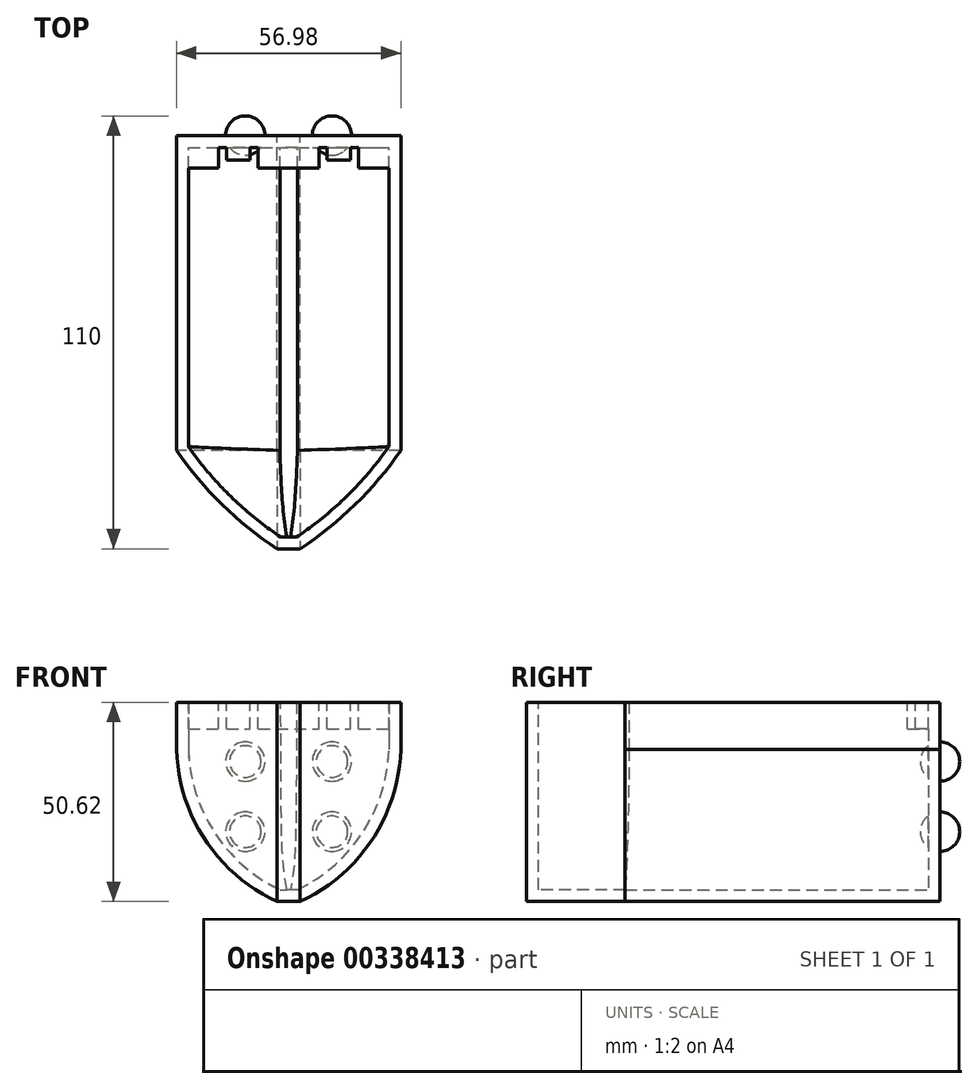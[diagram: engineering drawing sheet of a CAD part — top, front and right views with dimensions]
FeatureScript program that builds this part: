
annotation { "Feature Type Name" : "Feature", "Feature Type Description" : "" }
export const myFeature = defineFeature(function(context is Context, id is Id, definition is map)
    precondition{}
    {
        {
            var Q0;
            Q0=qCreatedBy(makeId("Front.planeOp"),FACE);
            var sketch = newSketch(context, id + "F0", { "sketchPlane" : qUnion([Q0])});
            skLineSegment(sketch, "E0.bottom", {"start": v(0, 23.95) * mm, "end": v(-28.49, 23.95) * mm});
            skLineSegment(sketch, "E0.top", {"start": v(0, -26.67) * mm, "end": v(-2.9, -26.67) * mm});
            skLineSegment(sketch, "E0.right", {"start": v(-28.49, 23.95) * mm, "end": v(-28.49, 11.98) * mm});
            skArc(sketch, "E1", {"start": v(-28.49, 11.98) * mm, "mid": v(-21.19, -10.99) * mm, "end": v(-2.9, -26.67) * mm});
            skArc(sketch, "E2.MirrorCS", {"start": v(28.49, 11.98) * mm, "mid": v(21.19, -10.99) * mm, "end": v(2.9, -26.67) * mm});
            skLineSegment(sketch, "E3.MirrorCS", {"start": v(28.49, 23.95) * mm, "end": v(28.49, 11.98) * mm});
            skLineSegment(sketch, "E4.MirrorCS", {"start": v(0, 23.95) * mm, "end": v(28.49, 23.95) * mm});
            skLineSegment(sketch, "E5.MirrorCS", {"start": v(0, -26.67) * mm, "end": v(2.9, -26.67) * mm});
            skPoint(sketch, "E6.orphan", {"position": v(-28.49, -26.67) * mm});
            skPoint(sketch, "E7.orphan", {"position": v(28.49, -26.67) * mm});
            skSolve(sketch);
        }
        {
            var Q0;
            Q0=makeQuery(id+"F0.imprint","IMPRINT",FACE,{"disambiguationData":[TD([[makeQuery(id+"F0.imprint","IMPRINT",EDGE,{"derivedFrom":sQuery(id+"F0.wireOp",EDGE,"E0.bottom")}),1.0]])]});
            extrude(context, id + "F1", {"entities" : qUnion([Q0]), "depth" : 80 * mm});
        }
        {
            var Q0;
            Q0=makeQuery(id+"F1.opExtrude","CAP_FACE",FACE,{"disambiguationData":[OSD([sQuery(id+"F0.wireOp",EDGE,"E0.bottom"),sQuery(id+"F0.wireOp",EDGE,"E0.top"),sQuery(id+"F0.wireOp",EDGE,"E0.right"),sQuery(id+"F0.wireOp",EDGE,"E1"),sQuery(id+"F0.wireOp",EDGE,"E2.MirrorCS"),sQuery(id+"F0.wireOp",EDGE,"E3.MirrorCS"),sQuery(id+"F0.wireOp",EDGE,"E4.MirrorCS"),sQuery(id+"F0.wireOp",EDGE,"E5.MirrorCS")])],"isStart":false});
            cPlane(context, id + "F2", {"entities" : qUnion([Q0]), "cplaneType" : CPlaneType.OFFSET, "offset" : 25 * mm, "width" : 150 * mm, "height" : 150 * mm});
        }
        {
            var Q0;
            Q0=qCreatedBy(id+"F2.planeOp",FACE);
            var sketch = newSketch(context, id + "F3", { "sketchPlane" : qUnion([Q0])});
            skLineSegment(sketch, "E8.bottom", {"start": v(0, -26.67) * mm, "end": v(-2.9, -26.67) * mm});
            skLineSegment(sketch, "E8.top", {"start": v(0, 23.95) * mm, "end": v(-2.9, 23.95) * mm});
            skLineSegment(sketch, "E8.right", {"start": v(-2.9, -26.67) * mm, "end": v(-2.9, 23.95) * mm});
            skLineSegment(sketch, "E9.MirrorCS", {"start": v(2.9, -26.67) * mm, "end": v(2.9, 23.95) * mm});
            skLineSegment(sketch, "E10.MirrorCS", {"start": v(0, -26.67) * mm, "end": v(2.9, -26.67) * mm});
            skLineSegment(sketch, "E11.MirrorCS", {"start": v(0, 23.95) * mm, "end": v(2.9, 23.95) * mm});
            skSolve(sketch);
        }
        {
            var Q0;
            Q0=makeQuery(id+"F1.opExtrude","SWEPT_FACE",FACE,{"disambiguationData":[OSD([sQuery(id+"F0.wireOp",EDGE,"E0.bottom"),sQuery(id+"F0.wireOp",EDGE,"E4.MirrorCS")])]});
            cPlane(context, id + "F4", {"entities" : qUnion([Q0]), "cplaneType" : CPlaneType.OFFSET, "offset" : 0 * mm, "width" : 150 * mm, "height" : 150 * mm});
        }
        {
            var Q0;
            Q0=qCreatedBy(id+"F4.planeOp",FACE);
            var sketch = newSketch(context, id + "F5", { "sketchPlane" : qUnion([Q0])});
            skArc(sketch, "E12", {"start": v(-28.49, -80) * mm, "mid": v(-16.9, -93.73) * mm, "end": v(-2.9, -105) * mm});
            skLineSegment(sketch, "E13", {"start": v(0, -105.03) * mm, "end": v(0, -80.6) * mm, "construction": true});
            skArc(sketch, "E14.MirrorCS", {"start": v(28.49, -80) * mm, "mid": v(16.9, -93.73) * mm, "end": v(2.9, -105) * mm});
            skSolve(sketch);
        }
        {
            var Q0;
            Q0=makeQuery(id+"F1.opExtrude","SWEPT_FACE",FACE,{"disambiguationData":[OSD([sQuery(id+"F0.wireOp",EDGE,"E0.top"),sQuery(id+"F0.wireOp",EDGE,"E5.MirrorCS")])]});
            cPlane(context, id + "F6", {"entities" : qUnion([Q0]), "cplaneType" : CPlaneType.OFFSET, "offset" : 0 * mm, "width" : 150 * mm, "height" : 150 * mm});
        }
        {
            var Q0;
            Q0=qCreatedBy(id+"F6.planeOp",FACE);
            var sketch = newSketch(context, id + "F7", { "sketchPlane" : qUnion([Q0])});
            skLineSegment(sketch, "E15", {"start": v(-2.9, 80) * mm, "end": v(-2.9, 105) * mm});
            skLineSegment(sketch, "E16", {"start": v(2.9, 80) * mm, "end": v(2.9, 105) * mm});
            skSolve(sketch);
        }
        {
            var Q1;
            Q1=makeQuery(id+"F1.opExtrude","CAP_FACE",FACE,{"disambiguationData":[OSD([sQuery(id+"F0.wireOp",EDGE,"E0.bottom"),sQuery(id+"F0.wireOp",EDGE,"E0.top"),sQuery(id+"F0.wireOp",EDGE,"E0.right"),sQuery(id+"F0.wireOp",EDGE,"E1"),sQuery(id+"F0.wireOp",EDGE,"E2.MirrorCS"),sQuery(id+"F0.wireOp",EDGE,"E3.MirrorCS"),sQuery(id+"F0.wireOp",EDGE,"E4.MirrorCS"),sQuery(id+"F0.wireOp",EDGE,"E5.MirrorCS")])],"isStart":false});
            var Q2;
            Q2=makeQuery(id+"F3.imprint","IMPRINT",FACE,{"disambiguationData":[TD([[makeQuery(id+"F3.imprint","IMPRINT",EDGE,{"derivedFrom":sQuery(id+"F3.wireOp",EDGE,"E8.bottom")}),-1.0]])]});
            var Q3;
            Q3=sQuery(id+"F5.wireOp",EDGE,"E12");
            var Q4;
            Q4=sQuery(id+"F5.wireOp",EDGE,"E14.MirrorCS");
            var Q5;
            Q5=sQuery(id+"F7.wireOp",EDGE,"E16");
            var Q6;
            Q6=sQuery(id+"F7.wireOp",EDGE,"E15");
            loft(context, id + "F8", {"operationType" : NewBodyOperationType.ADD, "addGuides" : true, "sheetProfilesArray" : [{ "sheetProfileEntities" : qUnion([Q1]) }, { "sheetProfileEntities" : qUnion([Q2]) }], "guidesArray" : [{ "guideEntities" : qUnion([Q3]), "guideDerivativeType" : LoftGuideDerivativeType.DEFAULT, "guideDerivativeMagnitude" : 1 }, { "guideEntities" : qUnion([Q4]), "guideDerivativeType" : LoftGuideDerivativeType.DEFAULT, "guideDerivativeMagnitude" : 1 }, { "guideEntities" : qUnion([Q5]), "guideDerivativeType" : LoftGuideDerivativeType.DEFAULT, "guideDerivativeMagnitude" : 1 }, { "guideEntities" : qUnion([Q6]), "guideDerivativeType" : LoftGuideDerivativeType.DEFAULT, "guideDerivativeMagnitude" : 1 }]});
        }
        {
            var Q0;
            {var subQ0=sQuery(id+"F0.wireOp",EDGE,"E4.MirrorCS");var subQ1=sQuery(id+"F0.wireOp",EDGE,"E0.bottom");Q0=makeQuery(id+"F8.boolean.opBoolean","MERGE",FACE,{"derivedFrom":[makeQuery(id+"F1.opExtrude","SWEPT_FACE",FACE,{"disambiguationData":[OSD([subQ1,subQ0])]}),makeQuery(id+"F8.opLoft","SWEPT_FACE",FACE,{"disambiguationData":[OSD([subQ1,subQ0,sQuery(id+"F3.wireOp",EDGE,"E8.top"),sQuery(id+"F3.wireOp",EDGE,"E11.MirrorCS"),sQuery(id+"F5.wireOp",EDGE,"E14.MirrorCS")])]})]});}
            shell(context, id + "F9", {"entities" : qUnion([Q0]), "thickness" : 3 * mm});
        }
        {
            var Q0;
            {var subQ0=sQuery(id+"F0.wireOp",EDGE,"E4.MirrorCS");var subQ1=sQuery(id+"F0.wireOp",EDGE,"E0.bottom");Q0=makeQuery(id+"F8.boolean.opBoolean","MERGE",FACE,{"derivedFrom":[makeQuery(id+"F1.opExtrude","SWEPT_FACE",FACE,{"disambiguationData":[OSD([subQ1,subQ0])]}),makeQuery(id+"F8.opLoft","SWEPT_FACE",FACE,{"disambiguationData":[OSD([subQ1,subQ0,sQuery(id+"F3.wireOp",EDGE,"E8.top"),sQuery(id+"F3.wireOp",EDGE,"E11.MirrorCS"),sQuery(id+"F5.wireOp",EDGE,"E14.MirrorCS")])]})]});}
            var sketch = newSketch(context, id + "F10", { "sketchPlane" : qUnion([Q0])});
            skLineSegment(sketch, "E17.bottom", {"start": v(-25.49, -3) * mm, "end": v(25.49, -3) * mm});
            skLineSegment(sketch, "E17.top", {"start": v(-25.49, -8.24) * mm, "end": v(25.49, -8.24) * mm});
            skLineSegment(sketch, "E17.left", {"start": v(-25.49, -3) * mm, "end": v(-25.49, -8.24) * mm});
            skLineSegment(sketch, "E17.right", {"start": v(25.49, -3) * mm, "end": v(25.49, -8.24) * mm});
            skSolve(sketch);
        }
        {
            var Q0;
            Q0=makeQuery(id+"F10.imprint","IMPRINT",FACE,{"disambiguationData":[TD([[makeQuery(id+"F10.imprint","IMPRINT",EDGE,{"derivedFrom":sQuery(id+"F10.wireOp",EDGE,"E17.bottom")}),-1.0]])]});
            extrude(context, id + "F11", {"entities" : qUnion([Q0]), "operationType" : NewBodyOperationType.ADD, "oppositeDirection" : true, "depth" : 6.8 * mm});
        }
        {
            var Q0;
            {var subQ0=sQuery(id+"F0.wireOp",EDGE,"E4.MirrorCS");var subQ1=sQuery(id+"F0.wireOp",EDGE,"E0.bottom");Q0=makeQuery(id+"F11.boolean.opBoolean","MERGE",FACE,{"derivedFrom":[makeQuery(id+"F8.boolean.opBoolean","MERGE",FACE,{"derivedFrom":[makeQuery(id+"F1.opExtrude","SWEPT_FACE",FACE,{"disambiguationData":[OSD([subQ1,subQ0])]}),makeQuery(id+"F8.opLoft","SWEPT_FACE",FACE,{"disambiguationData":[OSD([subQ1,subQ0,sQuery(id+"F3.wireOp",EDGE,"E8.top"),sQuery(id+"F3.wireOp",EDGE,"E11.MirrorCS"),sQuery(id+"F5.wireOp",EDGE,"E14.MirrorCS")])]})]}),makeQuery(id+"F11.opExtrude","CAP_FACE",FACE,{"disambiguationData":[OSD([sQuery(id+"F10.wireOp",EDGE,"E17.bottom"),sQuery(id+"F10.wireOp",EDGE,"E17.top"),sQuery(id+"F10.wireOp",EDGE,"E17.left"),sQuery(id+"F10.wireOp",EDGE,"E17.right")])],"isStart":true})]});}
            var sketch = newSketch(context, id + "F12", { "sketchPlane" : qUnion([Q0])});
            skLineSegment(sketch, "E18", {"start": v(0, 0) * mm, "end": v(0, -30.47) * mm, "construction": true});
            skPoint(sketch, "E18.endSnap0", {"position": v(0, 0) * mm});
            skLineSegment(sketch, "E19.bottom", {"start": v(-7.74, -8.24) * mm, "end": v(-17.74, -8.24) * mm});
            skLineSegment(sketch, "E19.top", {"start": v(-7.74, -3) * mm, "end": v(-9.74, -3) * mm});
            skLineSegment(sketch, "E19.left", {"start": v(-7.74, -8.24) * mm, "end": v(-7.74, -3) * mm});
            skLineSegment(sketch, "E19.right", {"start": v(-17.74, -8.24) * mm, "end": v(-17.74, -3) * mm});
            skLineSegment(sketch, "E20.top", {"start": v(-9.74, -6.24) * mm, "end": v(-15.74, -6.24) * mm});
            skLineSegment(sketch, "E20.left", {"start": v(-9.74, -3) * mm, "end": v(-9.74, -6.24) * mm});
            skLineSegment(sketch, "E20.right", {"start": v(-15.74, -3) * mm, "end": v(-15.74, -6.24) * mm});
            skLineSegment(sketch, "E21.trimOffspring", {"start": v(-15.74, -3) * mm, "end": v(-17.74, -3) * mm});
            skLineSegment(sketch, "E22.MirrorCS", {"start": v(7.74, -8.24) * mm, "end": v(7.74, -3) * mm});
            skLineSegment(sketch, "E23.MirrorCS", {"start": v(7.74, -3) * mm, "end": v(9.74, -3) * mm});
            skLineSegment(sketch, "E24.MirrorCS", {"start": v(9.74, -3) * mm, "end": v(9.74, -6.24) * mm});
            skLineSegment(sketch, "E25.MirrorCS", {"start": v(9.74, -6.24) * mm, "end": v(15.74, -6.24) * mm});
            skLineSegment(sketch, "E26.MirrorCS", {"start": v(7.74, -8.24) * mm, "end": v(17.74, -8.24) * mm});
            skLineSegment(sketch, "E27.MirrorCS", {"start": v(17.74, -8.24) * mm, "end": v(17.74, -3) * mm});
            skLineSegment(sketch, "E28.MirrorCS", {"start": v(15.74, -3) * mm, "end": v(17.74, -3) * mm});
            skLineSegment(sketch, "E29.MirrorCS", {"start": v(15.74, -3) * mm, "end": v(15.74, -6.24) * mm});
            skSolve(sketch);
        }
        {
            var Q0;
            Q0=makeQuery(id+"F12.imprint","IMPRINT",FACE,{"disambiguationData":[TD([[makeQuery(id+"F12.imprint","IMPRINT",EDGE,{"derivedFrom":sQuery(id+"F12.wireOp",EDGE,"E22.MirrorCS")}),-1.0]])]});
            var Q1;
            Q1=makeQuery(id+"F12.imprint","IMPRINT",FACE,{"disambiguationData":[TD([[makeQuery(id+"F12.imprint","IMPRINT",EDGE,{"derivedFrom":sQuery(id+"F12.wireOp",EDGE,"E19.bottom")}),1.0]])]});
            extrude(context, id + "F13", {"entities" : qUnion([Q0, Q1]), "operationType" : NewBodyOperationType.REMOVE, "oppositeDirection" : true, "depth" : 25 * mm});
        }
        {
            var Q0;
            Q0=makeQuery(id+"F1.opExtrude","CAP_FACE",FACE,{"disambiguationData":[OSD([sQuery(id+"F0.wireOp",EDGE,"E0.bottom"),sQuery(id+"F0.wireOp",EDGE,"E0.top"),sQuery(id+"F0.wireOp",EDGE,"E0.right"),sQuery(id+"F0.wireOp",EDGE,"E1"),sQuery(id+"F0.wireOp",EDGE,"E2.MirrorCS"),sQuery(id+"F0.wireOp",EDGE,"E3.MirrorCS"),sQuery(id+"F0.wireOp",EDGE,"E4.MirrorCS"),sQuery(id+"F0.wireOp",EDGE,"E5.MirrorCS")])],"isStart":true});
            var sketch = newSketch(context, id + "F14", { "sketchPlane" : qUnion([Q0])});
            skArc(sketch, "E30", {"start": v(-11, 13.92) * mm, "mid": v(-16, 8.92) * mm, "end": v(-11, 3.92) * mm});
            skLineSegment(sketch, "E31", {"start": v(-15.08, 0) * mm, "end": v(0, 0) * mm, "construction": true});
            skLineSegment(sketch, "E32", {"start": v(0, 10.01) * mm, "end": v(0, 0) * mm, "construction": true});
            skLineSegment(sketch, "E33", {"start": v(-11, 8.92) * mm, "end": v(-11, 3.92) * mm});
            skLineSegment(sketch, "E34", {"start": v(-11, 3.92) * mm, "end": v(-11, 13.92) * mm});
            skLineSegment(sketch, "E35.MirrorCS", {"start": v(-11, -3.92) * mm, "end": v(-11, -13.92) * mm});
            skArc(sketch, "E36.MirrorCS", {"start": v(-11, -13.92) * mm, "mid": v(-16, -8.92) * mm, "end": v(-11, -3.92) * mm});
            skSolve(sketch);
        }
        {
            var Q0;
            Q0=qSketchRegion(id+"F14",true);
            var Q1;
            Q1=sQuery(id+"F14.wireOp",EDGE,"E34");
            revolve(context, id + "F15", {"operationType" : NewBodyOperationType.ADD, "entities" : qUnion([Q0]), "axis" : qUnion([Q1]), "revolveType" : RevolveType.FULL});
        }
        {
            var Q0;
            Q0=makeQuery(id+"F1.opExtrude","SWEPT_BODY",BODY,{"disambiguationData":[OSD([sQuery(id+"F0.wireOp",EDGE,"E0.bottom"),sQuery(id+"F0.wireOp",EDGE,"E0.top"),sQuery(id+"F0.wireOp",EDGE,"E0.right"),sQuery(id+"F0.wireOp",EDGE,"E1"),sQuery(id+"F0.wireOp",EDGE,"E2.MirrorCS"),sQuery(id+"F0.wireOp",EDGE,"E3.MirrorCS"),sQuery(id+"F0.wireOp",EDGE,"E4.MirrorCS"),sQuery(id+"F0.wireOp",EDGE,"E5.MirrorCS")])]});
            var Q1;
            Q1=qCreatedBy(makeId("Right.planeOp"),FACE);
            mirror(context, id + "F16", {"operationType" : NewBodyOperationType.ADD, "entities" : qUnion([Q0]), "mirrorPlane" : qUnion([Q1])});
        }
    });
